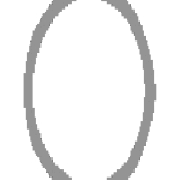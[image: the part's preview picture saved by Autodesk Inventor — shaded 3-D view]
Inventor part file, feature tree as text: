
AUTODESK INVENTOR PART (.ipt)
format: ipt  version: 2021 (Build 250183000, 183)  size: 109,568 bytes
history: native  units: in
note: dims shown in document units (in); Inventor stores cm internally (conversion verified against a paired STEP export)
features: other x4, sketch x3, plane x1
ambient origin geometry x8: Origin, YZ Plane, XZ Plane, XY Plane, X Axis, Y Axis, Z Axis, Center Point
bodies: Solid1 (feature_tree), Body (feature_tree)
feature tree (8):
  other  "Driven Length"
  other  "Frame Generator"
  other  "Start Plane"
  other  "End Plane"
  sketch  "Sketch"  dims[d2=14.3527in d4=-0.0in d5=14.3527in d6=0.12in d7=0.0in d8=90.0deg d9=14.3527in]
  sketch  "Sketch2"  dims[d0=1.0in]
  plane  "Work Plane3"
  sketch  "Sketch3"  dims[d1=0.065in]
